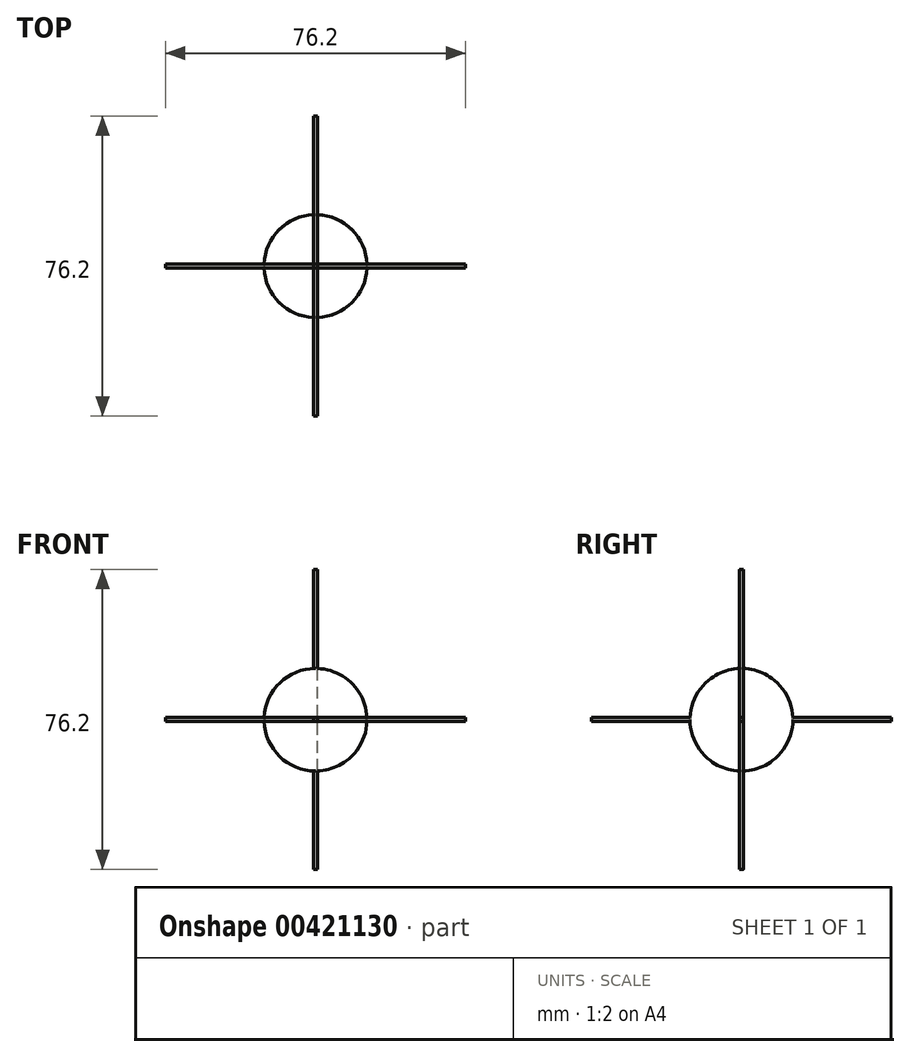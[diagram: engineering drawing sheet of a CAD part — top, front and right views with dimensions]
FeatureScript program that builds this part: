
annotation { "Feature Type Name" : "Feature", "Feature Type Description" : "" }
export const myFeature = defineFeature(function(context is Context, id is Id, definition is map)
    precondition{}
    {
        {
            var Q0;
            Q0=qCreatedBy(makeId("Front.planeOp"),FACE);
            var sketch = newSketch(context, id + "F0", { "sketchPlane" : qUnion([Q0])});
            skArc(sketch, "E0", {"start": v(0, 12.96) * mm, "mid": v(13.07, -0.06) * mm, "end": v(0, -13.09) * mm});
            skLineSegment(sketch, "E1", {"start": v(0, 25.15) * mm, "end": v(0, 5.08) * mm, "construction": true});
            skSolve(sketch);
        }
        {
            var Q0;
            Q0=sQuery(id+"F0.wireOp",EDGE,"E1");
            var Q1;
            Q1=sQuery(id+"F0.wireOp",EDGE,"E0");
            var Q2;
            Q2=sQuery(id+"F0.wireOp",EDGE,"E1");
            revolve(context, id + "F1", {"bodyType" : ToolBodyType.SURFACE, "surfaceEntities" : qUnion([Q0, Q1]), "axis" : qUnion([Q2]), "revolveType" : RevolveType.FULL});
        }
        {
            var Q0;
            Q0=qCreatedBy(makeId("Front.planeOp"),FACE);
            var sketch = newSketch(context, id + "F2", { "sketchPlane" : qUnion([Q0])});
            skCircle(sketch, "E2", {"center": v(0, 0) * mm, "radius": 0.47 * mm});
            skSolve(sketch);
        }
        {
            var Q0;
            Q0=sQuery(id+"F2.wireOp",EDGE,"E2");
            extrude(context, id + "F3", {"bodyType" : ToolBodyType.SURFACE, "surfaceEntities" : qUnion([Q0]), "endBound" : BoundingType.SYMMETRIC, "depth" : 76.2 * mm});
        }
        {
            var Q0;
            Q0=qCreatedBy(makeId("Top.planeOp"),FACE);
            var sketch = newSketch(context, id + "F4", { "sketchPlane" : qUnion([Q0])});
            skCircle(sketch, "E3", {"center": v(0, 0) * mm, "radius": 0.47 * mm});
            skSolve(sketch);
        }
        {
            var Q0;
            Q0=sQuery(id+"F4.wireOp",EDGE,"E3");
            extrude(context, id + "F5", {"bodyType" : ToolBodyType.SURFACE, "surfaceEntities" : qUnion([Q0]), "endBound" : BoundingType.SYMMETRIC, "depth" : 76.2 * mm});
        }
        {
            var Q0;
            Q0=qCreatedBy(makeId("Right.planeOp"),FACE);
            var sketch = newSketch(context, id + "F6", { "sketchPlane" : qUnion([Q0])});
            skCircle(sketch, "E4", {"center": v(0, 0.01) * mm, "radius": 0.47 * mm});
            skSolve(sketch);
        }
        {
            var Q0;
            Q0=sQuery(id+"F6.wireOp",EDGE,"E4");
            extrude(context, id + "F7", {"bodyType" : ToolBodyType.SURFACE, "surfaceEntities" : qUnion([Q0]), "endBound" : BoundingType.SYMMETRIC, "depth" : 76.2 * mm});
        }
    });
